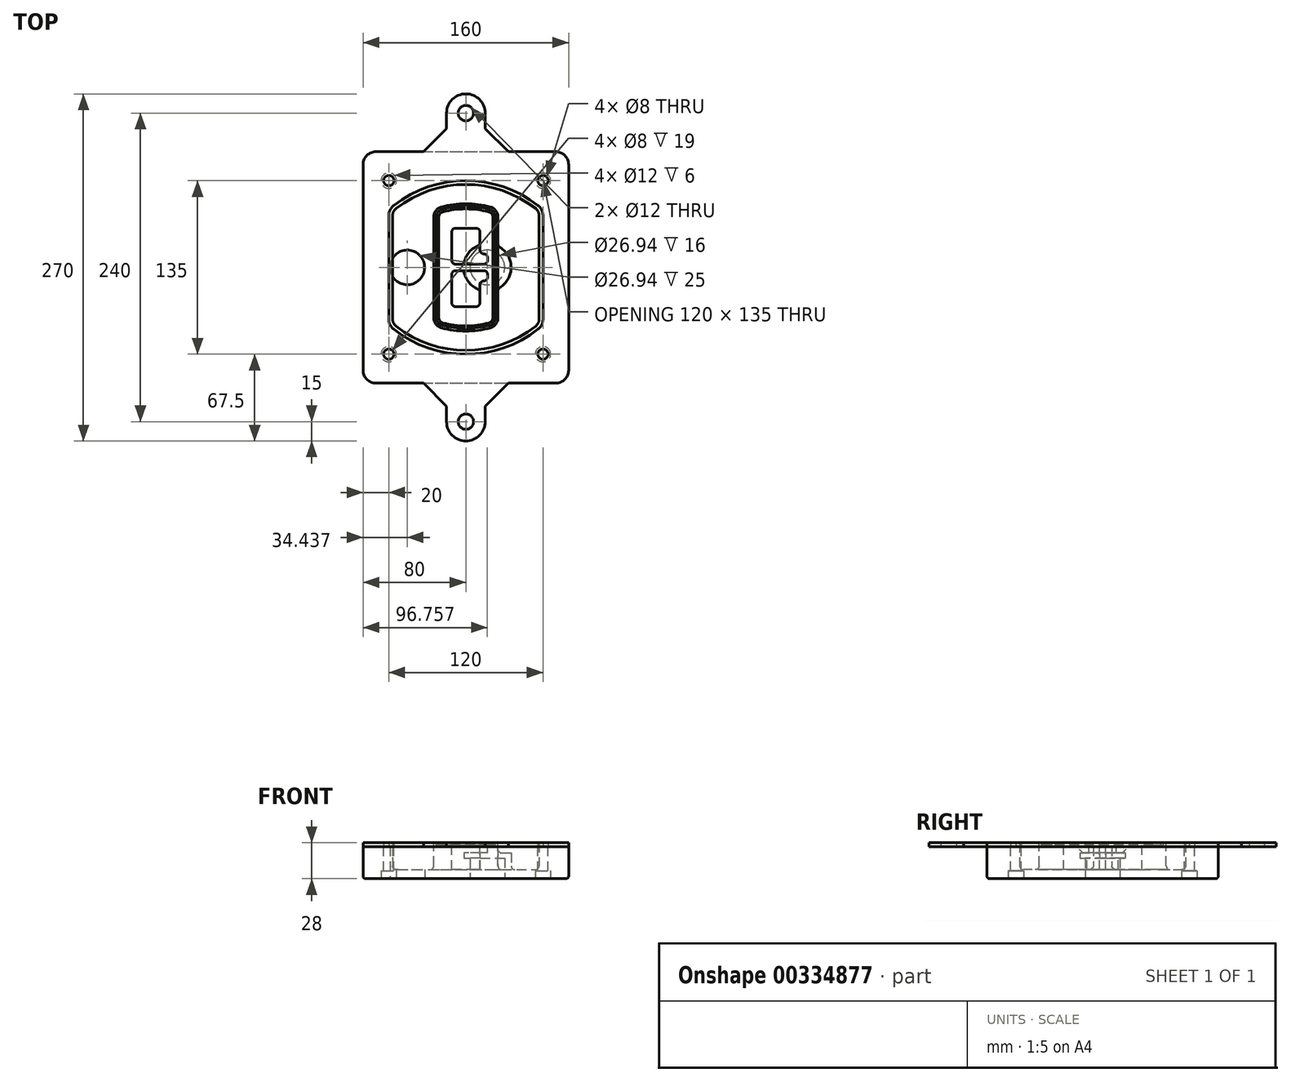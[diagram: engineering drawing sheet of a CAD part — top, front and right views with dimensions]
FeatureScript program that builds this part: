
annotation { "Feature Type Name" : "Feature", "Feature Type Description" : "" }
export const myFeature = defineFeature(function(context is Context, id is Id, definition is map)
    precondition{}
    {
        {
            var Q0;
            Q0=qCreatedBy(makeId("Top.planeOp"),FACE);
            var sketch = newSketch(context, id + "F0", { "sketchPlane" : qUnion([Q0])});
            skPoint(sketch, "E0.rect.middle", {"position": v(0, 0) * mm});
            skLineSegment(sketch, "E1.bottom", {"start": v(-70, -90) * mm, "end": v(70, -90) * mm});
            skLineSegment(sketch, "E1.top", {"start": v(-70, 90) * mm, "end": v(70, 90) * mm});
            skLineSegment(sketch, "E1.left", {"start": v(-80, -80) * mm, "end": v(-80, 80) * mm});
            skLineSegment(sketch, "E1.right", {"start": v(80, -80) * mm, "end": v(80, 80) * mm});
            skLineSegment(sketch, "E2", {"start": v(-80, 90) * mm, "end": v(80, -90) * mm, "construction": true});
            skLineSegment(sketch, "E3", {"start": v(80, 90) * mm, "end": v(-80, -90) * mm, "construction": true});
            skCircle(sketch, "E4", {"center": v(-60, 67.5) * mm, "radius": 4 * mm});
            skCircle(sketch, "E5", {"center": v(60, 67.5) * mm, "radius": 4 * mm});
            skCircle(sketch, "E6", {"center": v(60, -67.5) * mm, "radius": 4 * mm});
            skCircle(sketch, "E7", {"center": v(-60, -67.5) * mm, "radius": 4 * mm});
            skLineSegment(sketch, "E8", {"start": v(-60, 67.5) * mm, "end": v(60, 67.5) * mm, "construction": true});
            skLineSegment(sketch, "E9", {"start": v(60, 67.5) * mm, "end": v(60, -67.5) * mm, "construction": true});
            skLineSegment(sketch, "E10", {"start": v(60, -67.5) * mm, "end": v(-60, -67.5) * mm, "construction": true});
            skLineSegment(sketch, "E11", {"start": v(-60, -67.5) * mm, "end": v(-60, 67.5) * mm, "construction": true});
            skLineSegment(sketch, "E12", {"start": v(-60, 40.3) * mm, "end": v(-60, -40.3) * mm});
            skLineSegment(sketch, "E13", {"start": v(60, 40.3) * mm, "end": v(60, -40.3) * mm});
            skArc(sketch, "E14", {"start": v(56.15, 48.18) * mm, "mid": v(0, 67.5) * mm, "end": v(-56.15, 48.18) * mm});
            skArc(sketch, "E15", {"start": v(-56.15, -48.18) * mm, "mid": v(0, -67.5) * mm, "end": v(56.15, -48.18) * mm});
            skLineSegment(sketch, "E16", {"start": v(-60, 0) * mm, "end": v(60, 0) * mm, "construction": true});
            skPoint(sketch, "E17.visualSharp", {"position": v(-60, -45) * mm});
            skArc(sketch, "E17.filletArc", {"start": v(-60, -40.3) * mm, "mid": v(-58.99, -44.68) * mm, "end": v(-56.15, -48.18) * mm});
            skPoint(sketch, "E18.visualSharp", {"position": v(-60, 45) * mm});
            skArc(sketch, "E18.filletArc", {"start": v(-56.15, 48.18) * mm, "mid": v(-58.99, 44.68) * mm, "end": v(-60, 40.3) * mm});
            skPoint(sketch, "E19.visualSharp", {"position": v(60, 45) * mm});
            skArc(sketch, "E19.filletArc", {"start": v(60, 40.3) * mm, "mid": v(58.99, 44.68) * mm, "end": v(56.15, 48.18) * mm});
            skPoint(sketch, "E20.visualSharp", {"position": v(60, -45) * mm});
            skArc(sketch, "E20.filletArc", {"start": v(56.15, -48.18) * mm, "mid": v(58.99, -44.68) * mm, "end": v(60, -40.3) * mm});
            skPoint(sketch, "E21.visualSharp", {"position": v(-80, 90) * mm});
            skArc(sketch, "E21.filletArc", {"start": v(-70, 90) * mm, "mid": v(-77.07, 87.07) * mm, "end": v(-80, 80) * mm});
            skPoint(sketch, "E22.visualSharp", {"position": v(80, 90) * mm});
            skArc(sketch, "E22.filletArc", {"start": v(80, 80) * mm, "mid": v(77.07, 87.07) * mm, "end": v(70, 90) * mm});
            skPoint(sketch, "E23.visualSharp", {"position": v(80, -90) * mm});
            skArc(sketch, "E23.filletArc", {"start": v(70, -90) * mm, "mid": v(77.07, -87.07) * mm, "end": v(80, -80) * mm});
            skPoint(sketch, "E24.visualSharp", {"position": v(-80, -90) * mm});
            skArc(sketch, "E24.filletArc", {"start": v(-80, -80) * mm, "mid": v(-77.07, -87.07) * mm, "end": v(-70, -90) * mm});
            skArc(sketch, "E25.0", {"start": v(57, 40.3) * mm, "mid": v(56.3, 43.36) * mm, "end": v(54.3, 45.81) * mm});
            skLineSegment(sketch, "E25.1", {"start": v(57, 40.3) * mm, "end": v(57, -40.3) * mm});
            skArc(sketch, "E25.2", {"start": v(54.3, -45.81) * mm, "mid": v(56.3, -43.36) * mm, "end": v(57, -40.3) * mm});
            skArc(sketch, "E25.3", {"start": v(-54.3, -45.81) * mm, "mid": v(0, -64.5) * mm, "end": v(54.3, -45.81) * mm});
            skArc(sketch, "E25.4", {"start": v(-57, -40.3) * mm, "mid": v(-56.3, -43.36) * mm, "end": v(-54.3, -45.81) * mm});
            skArc(sketch, "E25.5", {"start": v(54.3, 45.81) * mm, "mid": v(0, 64.5) * mm, "end": v(-54.3, 45.81) * mm});
            skLineSegment(sketch, "E25.6", {"start": v(-57, 40.3) * mm, "end": v(-57, -40.3) * mm});
            skArc(sketch, "E25.7", {"start": v(-54.3, 45.81) * mm, "mid": v(-56.3, 43.36) * mm, "end": v(-57, 40.3) * mm});
            skArc(sketch, "E26.0", {"start": v(-58.62, 51.33) * mm, "mid": v(-62.58, 46.43) * mm, "end": v(-64, 40.3) * mm});
            skArc(sketch, "E26.1", {"start": v(58.62, 51.33) * mm, "mid": v(0, 71.5) * mm, "end": v(-58.62, 51.33) * mm});
            skArc(sketch, "E26.2", {"start": v(64, 40.3) * mm, "mid": v(62.58, 46.43) * mm, "end": v(58.62, 51.33) * mm});
            skLineSegment(sketch, "E26.3", {"start": v(64, 40.3) * mm, "end": v(64, -40.3) * mm});
            skArc(sketch, "E26.4", {"start": v(58.62, -51.33) * mm, "mid": v(62.58, -46.43) * mm, "end": v(64, -40.3) * mm});
            skLineSegment(sketch, "E26.5", {"start": v(-64, 40.3) * mm, "end": v(-64, -40.3) * mm});
            skArc(sketch, "E26.6", {"start": v(-58.62, -51.33) * mm, "mid": v(0, -71.5) * mm, "end": v(58.62, -51.33) * mm});
            skArc(sketch, "E26.7", {"start": v(-64, -40.3) * mm, "mid": v(-62.58, -46.43) * mm, "end": v(-58.62, -51.33) * mm});
            skSolve(sketch);
        }
        {
            var Q0;
            Q0=makeQuery(id+"F0.imprint","IMPRINT",FACE,{"disambiguationData":[TD([[makeQuery(id+"F0.imprint","IMPRINT",EDGE,{"derivedFrom":sQuery(id+"F0.wireOp",EDGE,"E1.bottom")}),1.0]])]});
            var Q1;
            Q1=makeQuery(id+"F0.imprint","IMPRINT",FACE,{"disambiguationData":[TD([[makeQuery(id+"F0.imprint","IMPRINT",EDGE,{"derivedFrom":sQuery(id+"F0.wireOp",EDGE,"E12")}),1.0]])]});
            var Q2;
            Q2=makeQuery(id+"F0.imprint","IMPRINT",FACE,{"disambiguationData":[TD([[makeQuery(id+"F0.imprint","IMPRINT",EDGE,{"derivedFrom":sQuery(id+"F0.wireOp",EDGE,"E25.0")}),1.0]])]});
            var Q3;
            Q3=makeQuery(id+"F0.imprint","IMPRINT",FACE,{"disambiguationData":[TD([[makeQuery(id+"F0.imprint","IMPRINT",EDGE,{"derivedFrom":sQuery(id+"F0.wireOp",EDGE,"E12")}),-1.0]])]});
            extrude(context, id + "F1", {"entities" : qUnion([Q0, Q1, Q2, Q3]), "oppositeDirection" : true, "depth" : 25 * mm});
        }
        {
            var Q0;
            Q0=makeQuery(id+"F0.imprint","IMPRINT",FACE,{"disambiguationData":[TD([[makeQuery(id+"F0.imprint","IMPRINT",EDGE,{"derivedFrom":sQuery(id+"F0.wireOp",EDGE,"E12")}),1.0]])]});
            extrude(context, id + "F2", {"entities" : qUnion([Q0]), "operationType" : NewBodyOperationType.ADD, "depth" : 3 * mm});
        }
        {
            var Q0;
            Q0=makeQuery(id+"F0.imprint","IMPRINT",FACE,{"disambiguationData":[TD([[makeQuery(id+"F0.imprint","IMPRINT",EDGE,{"derivedFrom":sQuery(id+"F0.wireOp",EDGE,"E25.0")}),1.0]])]});
            extrude(context, id + "F3", {"entities" : qUnion([Q0]), "operationType" : NewBodyOperationType.REMOVE, "oppositeDirection" : true, "depth" : 18 * mm});
        }
        {
            var Q0;
            Q0=makeQuery(id+"F2.opExtrude","CAP_FACE",FACE,{"disambiguationData":[OSD([sQuery(id+"F0.wireOp",EDGE,"E12"),sQuery(id+"F0.wireOp",EDGE,"E13"),sQuery(id+"F0.wireOp",EDGE,"E14"),sQuery(id+"F0.wireOp",EDGE,"E15"),sQuery(id+"F0.wireOp",EDGE,"E17.filletArc"),sQuery(id+"F0.wireOp",EDGE,"E18.filletArc"),sQuery(id+"F0.wireOp",EDGE,"E19.filletArc"),sQuery(id+"F0.wireOp",EDGE,"E20.filletArc"),sQuery(id+"F0.wireOp",EDGE,"E25.0"),sQuery(id+"F0.wireOp",EDGE,"E25.1"),sQuery(id+"F0.wireOp",EDGE,"E25.2"),sQuery(id+"F0.wireOp",EDGE,"E25.3"),sQuery(id+"F0.wireOp",EDGE,"E25.4"),sQuery(id+"F0.wireOp",EDGE,"E25.5"),sQuery(id+"F0.wireOp",EDGE,"E25.6"),sQuery(id+"F0.wireOp",EDGE,"E25.7")])],"isStart":false});
            var sketch = newSketch(context, id + "F4", { "sketchPlane" : qUnion([Q0])});
            skArc(sketch, "E27.0", {"start": v(-19.08, -46.97) * mm, "mid": v(0, -49.5) * mm, "end": v(19.08, -46.97) * mm});
            skArc(sketch, "E28.0", {"start": v(19.08, 46.97) * mm, "mid": v(0, 49.5) * mm, "end": v(-19.08, 46.97) * mm});
            skLineSegment(sketch, "E29", {"start": v(-25, 39.25) * mm, "end": v(-25, -39.25) * mm});
            skLineSegment(sketch, "E30", {"start": v(25, 39.25) * mm, "end": v(25, -39.25) * mm});
            skLineSegment(sketch, "E31", {"start": v(-25, 45.1) * mm, "end": v(25, 45.1) * mm, "construction": true});
            skLineSegment(sketch, "E32", {"start": v(-25, -45.1) * mm, "end": v(25, -45.1) * mm, "construction": true});
            skPoint(sketch, "E33.visualSharp", {"position": v(-25, 45.1) * mm});
            skArc(sketch, "E33.filletArc", {"start": v(-19.08, 46.97) * mm, "mid": v(-23.35, 44.11) * mm, "end": v(-25, 39.25) * mm});
            skPoint(sketch, "E34.visualSharp", {"position": v(25, 45.1) * mm});
            skArc(sketch, "E34.filletArc", {"start": v(25, 39.25) * mm, "mid": v(23.35, 44.11) * mm, "end": v(19.08, 46.97) * mm});
            skPoint(sketch, "E35.visualSharp", {"position": v(25, -45.1) * mm});
            skArc(sketch, "E35.filletArc", {"start": v(19.08, -46.97) * mm, "mid": v(23.35, -44.11) * mm, "end": v(25, -39.25) * mm});
            skPoint(sketch, "E36.visualSharp", {"position": v(-25, -45.1) * mm});
            skArc(sketch, "E36.filletArc", {"start": v(-25, -39.25) * mm, "mid": v(-23.35, -44.11) * mm, "end": v(-19.08, -46.97) * mm});
            skArc(sketch, "E37.0", {"start": v(54.3, 45.81) * mm, "mid": v(0, 64.5) * mm, "end": v(-54.3, 45.81) * mm});
            skArc(sketch, "E37.1", {"start": v(-54.3, 45.81) * mm, "mid": v(-56.3, 43.36) * mm, "end": v(-57, 40.3) * mm});
            skLineSegment(sketch, "E37.2", {"start": v(-57, 40.3) * mm, "end": v(-57, -40.3) * mm});
            skArc(sketch, "E37.3", {"start": v(-57, -40.3) * mm, "mid": v(-56.3, -43.36) * mm, "end": v(-54.3, -45.81) * mm});
            skArc(sketch, "E37.4", {"start": v(-54.3, -45.81) * mm, "mid": v(0, -64.5) * mm, "end": v(54.3, -45.81) * mm});
            skArc(sketch, "E37.5", {"start": v(54.3, -45.81) * mm, "mid": v(56.3, -43.36) * mm, "end": v(57, -40.3) * mm});
            skLineSegment(sketch, "E37.6", {"start": v(57, 40.3) * mm, "end": v(57, -40.3) * mm});
            skArc(sketch, "E37.7", {"start": v(57, 40.3) * mm, "mid": v(56.3, 43.36) * mm, "end": v(54.3, 45.81) * mm});
            skLineSegment(sketch, "E38.0", {"start": v(23, 39.25) * mm, "end": v(23, -39.25) * mm});
            skArc(sketch, "E38.1", {"start": v(18.56, -45.04) * mm, "mid": v(21.76, -42.9) * mm, "end": v(23, -39.25) * mm});
            skArc(sketch, "E38.2", {"start": v(-18.56, -45.04) * mm, "mid": v(0, -47.5) * mm, "end": v(18.56, -45.04) * mm});
            skArc(sketch, "E38.3", {"start": v(-23, -39.25) * mm, "mid": v(-21.76, -42.9) * mm, "end": v(-18.56, -45.04) * mm});
            skLineSegment(sketch, "E38.4", {"start": v(-23, 39.25) * mm, "end": v(-23, -39.25) * mm});
            skArc(sketch, "E38.5", {"start": v(23, 39.25) * mm, "mid": v(21.76, 42.9) * mm, "end": v(18.56, 45.04) * mm});
            skArc(sketch, "E38.6", {"start": v(-18.56, 45.04) * mm, "mid": v(-21.76, 42.9) * mm, "end": v(-23, 39.25) * mm});
            skArc(sketch, "E38.7", {"start": v(18.56, 45.04) * mm, "mid": v(0, 47.5) * mm, "end": v(-18.56, 45.04) * mm});
            skArc(sketch, "E39.0", {"start": v(21, 39.25) * mm, "mid": v(20.18, 41.68) * mm, "end": v(18.04, 43.1) * mm});
            skLineSegment(sketch, "E39.1", {"start": v(21, 39.25) * mm, "end": v(21, -39.25) * mm});
            skArc(sketch, "E39.2", {"start": v(18.04, -43.1) * mm, "mid": v(20.18, -41.68) * mm, "end": v(21, -39.25) * mm});
            skArc(sketch, "E39.3", {"start": v(-18.04, -43.1) * mm, "mid": v(0, -45.5) * mm, "end": v(18.04, -43.1) * mm});
            skArc(sketch, "E39.4", {"start": v(-21, -39.25) * mm, "mid": v(-20.18, -41.68) * mm, "end": v(-18.04, -43.1) * mm});
            skArc(sketch, "E39.5", {"start": v(18.04, 43.1) * mm, "mid": v(0, 45.5) * mm, "end": v(-18.04, 43.1) * mm});
            skLineSegment(sketch, "E39.6", {"start": v(-21, 39.25) * mm, "end": v(-21, -39.25) * mm});
            skArc(sketch, "E39.7", {"start": v(-18.04, 43.1) * mm, "mid": v(-20.18, 41.68) * mm, "end": v(-21, 39.25) * mm});
            skLineSegment(sketch, "E40", {"start": v(-25, 0) * mm, "end": v(25, 0) * mm, "construction": true});
            skLineSegment(sketch, "E41", {"start": v(-11, 5.5) * mm, "end": v(-11, 27.5) * mm});
            skLineSegment(sketch, "E42", {"start": v(-8, 30.5) * mm, "end": v(8, 30.5) * mm});
            skLineSegment(sketch, "E43", {"start": v(11, 27.5) * mm, "end": v(11, 13.5) * mm});
            skLineSegment(sketch, "E44", {"start": v(14, 10.5) * mm, "end": v(14, 10.5) * mm});
            skLineSegment(sketch, "E45", {"start": v(17, 7.5) * mm, "end": v(17, 5.5) * mm});
            skLineSegment(sketch, "E46", {"start": v(14, 2.5) * mm, "end": v(-8, 2.5) * mm});
            skPoint(sketch, "E47.visualSharp", {"position": v(-11, 30.5) * mm});
            skArc(sketch, "E47.filletArc", {"start": v(-8, 30.5) * mm, "mid": v(-10.12, 29.62) * mm, "end": v(-11, 27.5) * mm});
            skPoint(sketch, "E48.visualSharp", {"position": v(11, 30.5) * mm});
            skArc(sketch, "E48.filletArc", {"start": v(11, 27.5) * mm, "mid": v(10.12, 29.62) * mm, "end": v(8, 30.5) * mm});
            skPoint(sketch, "E49.visualSharp", {"position": v(11, 10.5) * mm});
            skArc(sketch, "E49.filletArc", {"start": v(11, 13.5) * mm, "mid": v(11.88, 11.38) * mm, "end": v(14, 10.5) * mm});
            skPoint(sketch, "E50.visualSharp", {"position": v(17, 10.5) * mm});
            skArc(sketch, "E50.filletArc", {"start": v(17, 7.5) * mm, "mid": v(16.12, 9.62) * mm, "end": v(14, 10.5) * mm});
            skPoint(sketch, "E51.visualSharp", {"position": v(17, 2.5) * mm});
            skArc(sketch, "E51.filletArc", {"start": v(14, 2.5) * mm, "mid": v(16.12, 3.38) * mm, "end": v(17, 5.5) * mm});
            skPoint(sketch, "E52.visualSharp", {"position": v(-11, 2.5) * mm});
            skArc(sketch, "E52.filletArc", {"start": v(-11, 5.5) * mm, "mid": v(-10.12, 3.38) * mm, "end": v(-8, 2.5) * mm});
            skLineSegment(sketch, "E53.0.MirrorCS", {"start": v(14, -2.5) * mm, "end": v(-8, -2.5) * mm});
            skArc(sketch, "E54.0.MirrorCS", {"start": v(-11, -5.5) * mm, "mid": v(-10.12, -3.38) * mm, "end": v(-8, -2.5) * mm});
            skLineSegment(sketch, "E55.0.MirrorCS", {"start": v(-11, -5.5) * mm, "end": v(-11, -27.5) * mm});
            skArc(sketch, "E56.0.MirrorCS", {"start": v(-8, -30.5) * mm, "mid": v(-10.12, -29.62) * mm, "end": v(-11, -27.5) * mm});
            skLineSegment(sketch, "E57.0.MirrorCS", {"start": v(-8, -30.5) * mm, "end": v(8, -30.5) * mm});
            skArc(sketch, "E58.0.MirrorCS", {"start": v(11, -27.5) * mm, "mid": v(10.12, -29.62) * mm, "end": v(8, -30.5) * mm});
            skLineSegment(sketch, "E59.0.MirrorCS", {"start": v(11, -27.5) * mm, "end": v(11, -13.5) * mm});
            skArc(sketch, "E60.0.MirrorCS", {"start": v(11, -13.5) * mm, "mid": v(11.88, -11.38) * mm, "end": v(14, -10.5) * mm});
            skArc(sketch, "E61.0.MirrorCS", {"start": v(17, -7.5) * mm, "mid": v(16.12, -9.62) * mm, "end": v(14, -10.5) * mm});
            skLineSegment(sketch, "E62.0.MirrorCS", {"start": v(17, -7.5) * mm, "end": v(17, -5.5) * mm});
            skArc(sketch, "E63.0.MirrorCS", {"start": v(14, -2.5) * mm, "mid": v(16.12, -3.38) * mm, "end": v(17, -5.5) * mm});
            skSolve(sketch);
        }
        {
            var Q0;
            Q0=makeQuery(id+"F4.imprint","IMPRINT",FACE,{"disambiguationData":[TD([[makeQuery(id+"F4.imprint","IMPRINT",EDGE,{"derivedFrom":sQuery(id+"F4.wireOp",EDGE,"E27.0")}),1.0]])]});
            var Q1;
            Q1=makeQuery(id+"F4.imprint","IMPRINT",FACE,{"disambiguationData":[TD([[makeQuery(id+"F4.imprint","IMPRINT",EDGE,{"derivedFrom":sQuery(id+"F4.wireOp",EDGE,"E38.0")}),-1.0]])]});
            var Q2;
            Q2=makeQuery(id+"F4.imprint","IMPRINT",FACE,{"disambiguationData":[TD([[makeQuery(id+"F4.imprint","IMPRINT",EDGE,{"derivedFrom":sQuery(id+"F4.wireOp",EDGE,"E39.0")}),1.0]])]});
            extrude(context, id + "F5", {"entities" : qUnion([Q0, Q1, Q2]), "operationType" : NewBodyOperationType.ADD, "endBound" : BoundingType.UP_TO_NEXT, "oppositeDirection" : true, "depth" : 25 * mm});
        }
        {
            var Q0;
            Q0=makeQuery(id+"F4.imprint","IMPRINT",FACE,{"disambiguationData":[TD([[makeQuery(id+"F4.imprint","IMPRINT",EDGE,{"derivedFrom":sQuery(id+"F4.wireOp",EDGE,"E38.0")}),-1.0]])]});
            extrude(context, id + "F6", {"entities" : qUnion([Q0]), "operationType" : NewBodyOperationType.REMOVE, "oppositeDirection" : true, "depth" : 2 * mm});
        }
        {
            var Q0;
            Q0=makeQuery(id+"F1.opExtrude","CAP_FACE",FACE,{"disambiguationData":[OSD([sQuery(id+"F0.wireOp",EDGE,"E1.bottom"),sQuery(id+"F0.wireOp",EDGE,"E1.top"),sQuery(id+"F0.wireOp",EDGE,"E1.left"),sQuery(id+"F0.wireOp",EDGE,"E1.right"),sQuery(id+"F0.wireOp",EDGE,"E4"),sQuery(id+"F0.wireOp",EDGE,"E5"),sQuery(id+"F0.wireOp",EDGE,"E6"),sQuery(id+"F0.wireOp",EDGE,"E7"),sQuery(id+"F0.wireOp",EDGE,"E21.filletArc"),sQuery(id+"F0.wireOp",EDGE,"E22.filletArc"),sQuery(id+"F0.wireOp",EDGE,"E23.filletArc"),sQuery(id+"F0.wireOp",EDGE,"E24.filletArc")])],"isStart":false});
            var sketch = newSketch(context, id + "F7", { "sketchPlane" : qUnion([Q0])});
            skCircle(sketch, "E64", {"center": v(16.76, 0) * mm, "radius": 13.47 * mm});
            skCircle(sketch, "E65", {"center": v(-45.56, 0) * mm, "radius": 13.47 * mm});
            skLineSegment(sketch, "E66", {"start": v(80, 0) * mm, "end": v(-80, 0) * mm});
            skCircle(sketch, "E67", {"center": v(16.76, 0) * mm, "radius": 18.47 * mm});
            skCircle(sketch, "E68", {"center": v(60, -67.5) * mm, "radius": 6 * mm});
            skCircle(sketch, "E69", {"center": v(-60, -67.5) * mm, "radius": 6 * mm});
            skCircle(sketch, "E70", {"center": v(-60, 67.5) * mm, "radius": 6 * mm});
            skCircle(sketch, "E71", {"center": v(60, 67.5) * mm, "radius": 6 * mm});
            skSolve(sketch);
        }
        {
            var Q0;
            {var subQ1=sQuery(id+"F7.wireOp",EDGE,"E66");var subQ4=sQuery(id+"F7.wireOp",EDGE,"E64");var subQ6=makeQuery(id+"F7.imprint","INTERSECT",VERTEX,{"disambiguationData":[OD(0.0)],"derivedFrom":[subQ4,subQ1]});Q0=makeQuery(id+"F7.imprint","IMPRINT",FACE,{"disambiguationData":[TD([[makeQuery(id+"F7.imprint","IMPRINT",EDGE,{"disambiguationData":[TD([[subQ6,-1.0]])],"derivedFrom":subQ4}),-1.0]])]});}
            var Q1;
            {var subQ0=sQuery(id+"F7.wireOp",EDGE,"E66");var subQ1=sQuery(id+"F7.wireOp",EDGE,"E64");var subQ3=makeQuery(id+"F7.imprint","INTERSECT",VERTEX,{"disambiguationData":[OD(0.0)],"derivedFrom":[subQ1,subQ0]});Q1=makeQuery(id+"F7.imprint","IMPRINT",FACE,{"disambiguationData":[TD([[makeQuery(id+"F7.imprint","IMPRINT",EDGE,{"disambiguationData":[TD([[subQ3,-1.0]])],"derivedFrom":subQ1}),1.0]])]});}
            var Q2;
            {var subQ0=sQuery(id+"F7.wireOp",EDGE,"E66");var subQ1=sQuery(id+"F7.wireOp",EDGE,"E64");var subQ3=makeQuery(id+"F7.imprint","INTERSECT",VERTEX,{"disambiguationData":[OD(0.0)],"derivedFrom":[subQ1,subQ0]});Q2=makeQuery(id+"F7.imprint","IMPRINT",FACE,{"disambiguationData":[TD([[makeQuery(id+"F7.imprint","IMPRINT",EDGE,{"disambiguationData":[TD([[subQ3,1.0]])],"derivedFrom":subQ1}),1.0]])]});}
            var Q3;
            {var subQ1=sQuery(id+"F7.wireOp",EDGE,"E66");var subQ4=sQuery(id+"F7.wireOp",EDGE,"E64");var subQ6=makeQuery(id+"F7.imprint","INTERSECT",VERTEX,{"disambiguationData":[OD(0.0)],"derivedFrom":[subQ4,subQ1]});Q3=makeQuery(id+"F7.imprint","IMPRINT",FACE,{"disambiguationData":[TD([[makeQuery(id+"F7.imprint","IMPRINT",EDGE,{"disambiguationData":[TD([[subQ6,1.0]])],"derivedFrom":subQ4}),-1.0]])]});}
            extrude(context, id + "F8", {"entities" : qUnion([Q0, Q1, Q2, Q3]), "operationType" : NewBodyOperationType.ADD, "oppositeDirection" : true, "depth" : 20 * mm});
        }
        {
            var Q0;
            {var subQ0=sQuery(id+"F7.wireOp",EDGE,"E66");var subQ1=sQuery(id+"F7.wireOp",EDGE,"E64");var subQ3=makeQuery(id+"F7.imprint","INTERSECT",VERTEX,{"disambiguationData":[OD(0.0)],"derivedFrom":[subQ1,subQ0]});Q0=makeQuery(id+"F7.imprint","IMPRINT",FACE,{"disambiguationData":[TD([[makeQuery(id+"F7.imprint","IMPRINT",EDGE,{"disambiguationData":[TD([[subQ3,-1.0]])],"derivedFrom":subQ1}),1.0]])]});}
            var Q1;
            {var subQ0=sQuery(id+"F7.wireOp",EDGE,"E66");var subQ1=sQuery(id+"F7.wireOp",EDGE,"E64");var subQ3=makeQuery(id+"F7.imprint","INTERSECT",VERTEX,{"disambiguationData":[OD(0.0)],"derivedFrom":[subQ1,subQ0]});Q1=makeQuery(id+"F7.imprint","IMPRINT",FACE,{"disambiguationData":[TD([[makeQuery(id+"F7.imprint","IMPRINT",EDGE,{"disambiguationData":[TD([[subQ3,1.0]])],"derivedFrom":subQ1}),1.0]])]});}
            extrude(context, id + "F9", {"entities" : qUnion([Q0, Q1]), "operationType" : NewBodyOperationType.REMOVE, "oppositeDirection" : true, "depth" : 16 * mm});
        }
        {
            var Q0;
            {var subQ0=sQuery(id+"F7.wireOp",EDGE,"E66");var subQ1=sQuery(id+"F7.wireOp",EDGE,"E65");var subQ3=makeQuery(id+"F7.imprint","INTERSECT",VERTEX,{"disambiguationData":[OD(0.0)],"derivedFrom":[subQ1,subQ0]});Q0=makeQuery(id+"F7.imprint","IMPRINT",FACE,{"disambiguationData":[TD([[makeQuery(id+"F7.imprint","IMPRINT",EDGE,{"disambiguationData":[TD([[subQ3,-1.0]])],"derivedFrom":subQ1}),1.0]])]});}
            var Q1;
            {var subQ0=sQuery(id+"F7.wireOp",EDGE,"E66");var subQ1=sQuery(id+"F7.wireOp",EDGE,"E65");var subQ3=makeQuery(id+"F7.imprint","INTERSECT",VERTEX,{"disambiguationData":[OD(0.0)],"derivedFrom":[subQ1,subQ0]});Q1=makeQuery(id+"F7.imprint","IMPRINT",FACE,{"disambiguationData":[TD([[makeQuery(id+"F7.imprint","IMPRINT",EDGE,{"disambiguationData":[TD([[subQ3,1.0]])],"derivedFrom":subQ1}),1.0]])]});}
            extrude(context, id + "F10", {"entities" : qUnion([Q0, Q1]), "operationType" : NewBodyOperationType.REMOVE, "oppositeDirection" : true, "depth" : 25 * mm});
        }
        {
            var Q0;
            Q0=makeQuery(id+"F7.imprint","IMPRINT",FACE,{"disambiguationData":[TD([[makeQuery(id+"F7.imprint","IMPRINT",EDGE,{"derivedFrom":sQuery(id+"F7.wireOp",EDGE,"E68")}),1.0]])]});
            var Q1;
            Q1=makeQuery(id+"F7.imprint","IMPRINT",FACE,{"disambiguationData":[TD([[makeQuery(id+"F7.imprint","IMPRINT",EDGE,{"derivedFrom":makeQuery(id+"F1.opExtrude","CAP_EDGE",EDGE,{"disambiguationData":[OSD([sQuery(id+"F0.wireOp",EDGE,"E5")])],"isStart":false})}),-1.0]])]});
            var Q2;
            Q2=makeQuery(id+"F7.imprint","IMPRINT",FACE,{"disambiguationData":[TD([[makeQuery(id+"F7.imprint","IMPRINT",EDGE,{"derivedFrom":sQuery(id+"F7.wireOp",EDGE,"E69")}),1.0]])]});
            var Q3;
            Q3=makeQuery(id+"F7.imprint","IMPRINT",FACE,{"disambiguationData":[TD([[makeQuery(id+"F7.imprint","IMPRINT",EDGE,{"derivedFrom":makeQuery(id+"F1.opExtrude","CAP_EDGE",EDGE,{"disambiguationData":[OSD([sQuery(id+"F0.wireOp",EDGE,"E4")])],"isStart":false})}),-1.0]])]});
            var Q4;
            Q4=makeQuery(id+"F7.imprint","IMPRINT",FACE,{"disambiguationData":[TD([[makeQuery(id+"F7.imprint","IMPRINT",EDGE,{"derivedFrom":sQuery(id+"F7.wireOp",EDGE,"E70")}),1.0]])]});
            var Q5;
            Q5=makeQuery(id+"F7.imprint","IMPRINT",FACE,{"disambiguationData":[TD([[makeQuery(id+"F7.imprint","IMPRINT",EDGE,{"derivedFrom":makeQuery(id+"F1.opExtrude","CAP_EDGE",EDGE,{"disambiguationData":[OSD([sQuery(id+"F0.wireOp",EDGE,"E7")])],"isStart":false})}),-1.0]])]});
            var Q6;
            Q6=makeQuery(id+"F7.imprint","IMPRINT",FACE,{"disambiguationData":[TD([[makeQuery(id+"F7.imprint","IMPRINT",EDGE,{"derivedFrom":sQuery(id+"F7.wireOp",EDGE,"E71")}),1.0]])]});
            var Q7;
            Q7=makeQuery(id+"F7.imprint","IMPRINT",FACE,{"disambiguationData":[TD([[makeQuery(id+"F7.imprint","IMPRINT",EDGE,{"derivedFrom":makeQuery(id+"F1.opExtrude","CAP_EDGE",EDGE,{"disambiguationData":[OSD([sQuery(id+"F0.wireOp",EDGE,"E6")])],"isStart":false})}),-1.0]])]});
            extrude(context, id + "F11", {"entities" : qUnion([Q0, Q1, Q2, Q3, Q4, Q5, Q6, Q7]), "operationType" : NewBodyOperationType.REMOVE, "oppositeDirection" : true, "depth" : 6 * mm});
        }
        {
            var Q0;
            Q0=makeQuery(id+"F9.boolean.opBoolean","COPY",FACE,{"derivedFrom":makeQuery(id+"F9.opExtrude","CAP_FACE",FACE,{"disambiguationData":[OSD([sQuery(id+"F7.wireOp",EDGE,"E64")])],"isStart":false})});
            var sketch = newSketch(context, id + "F12", { "sketchPlane" : qUnion([Q0])});
            skArc(sketch, "E72.0", {"start": v(11, 17.55) * mm, "mid": v(2.57, 11.82) * mm, "end": v(-1.54, 2.5) * mm});
            skArc(sketch, "E72.1", {"start": v(-1.54, -2.5) * mm, "mid": v(2.57, -11.82) * mm, "end": v(11, -17.55) * mm});
            skLineSegment(sketch, "E73", {"start": v(-1.54, -2.5) * mm, "end": v(14, -2.5) * mm});
            skLineSegment(sketch, "E74.0", {"start": v(14, 2.5) * mm, "end": v(-1.54, 2.5) * mm});
            skArc(sketch, "E74.1", {"start": v(14, 2.5) * mm, "mid": v(16.12, 3.38) * mm, "end": v(17, 5.5) * mm});
            skLineSegment(sketch, "E74.2", {"start": v(17, 7.5) * mm, "end": v(17, 5.5) * mm});
            skArc(sketch, "E74.3", {"start": v(17, 7.5) * mm, "mid": v(16.12, 9.62) * mm, "end": v(14, 10.5) * mm});
            skArc(sketch, "E74.4", {"start": v(11, 13.5) * mm, "mid": v(11.88, 11.38) * mm, "end": v(14, 10.5) * mm});
            skLineSegment(sketch, "E74.5", {"start": v(11, 17.55) * mm, "end": v(11, 13.5) * mm});
            skLineSegment(sketch, "E74.7", {"start": v(14, -2.5) * mm, "end": v(-1.54, -2.5) * mm});
            skArc(sketch, "E74.8", {"start": v(14, -2.5) * mm, "mid": v(16.12, -3.38) * mm, "end": v(17, -5.5) * mm});
            skLineSegment(sketch, "E74.9", {"start": v(17, -7.5) * mm, "end": v(17, -5.5) * mm});
            skArc(sketch, "E74.10", {"start": v(17, -7.5) * mm, "mid": v(16.12, -9.62) * mm, "end": v(14, -10.5) * mm});
            skArc(sketch, "E74.11", {"start": v(11, -13.5) * mm, "mid": v(11.88, -11.38) * mm, "end": v(14, -10.5) * mm});
            skLineSegment(sketch, "E74.12", {"start": v(11, -17.55) * mm, "end": v(11, -13.5) * mm});
            skPoint(sketch, "E75.orphan", {"position": v(11, -27.5) * mm});
            skPoint(sketch, "E76.orphan", {"position": v(-8, -2.5) * mm});
            skPoint(sketch, "E77.orphan", {"position": v(-8, 2.5) * mm});
            skPoint(sketch, "E78.orphan", {"position": v(11, 27.5) * mm});
            skSolve(sketch);
        }
        {
            var Q0;
            {var subQ7=sQuery(id+"F12.wireOp",EDGE,"E72.0");var subQ14=sQuery(id+"F12.wireOp",EDGE,"E72.1");var subQ16=sQuery(id+"F12.wireOp",EDGE,"E74.1");var subQ18=sQuery(id+"F12.wireOp",EDGE,"E74.8");Q0=qUnion([makeQuery(id+"F12.imprint","IMPRINT",FACE,{"disambiguationData":[TD([[makeQuery(id+"F12.imprint","IMPRINT",EDGE,{"derivedFrom":subQ7}),1.0]])]}),makeQuery(id+"F12.imprint","IMPRINT",FACE,{"disambiguationData":[TD([[makeQuery(id+"F12.imprint","IMPRINT",EDGE,{"derivedFrom":subQ14}),1.0]])]}),makeQuery(id+"F12.imprint","IMPRINT",FACE,{"disambiguationData":[TD([[makeQuery(id+"F12.imprint","IMPRINT",EDGE,{"derivedFrom":subQ16}),1.0]])]}),makeQuery(id+"F12.imprint","IMPRINT",FACE,{"disambiguationData":[TD([[makeQuery(id+"F12.imprint","IMPRINT",EDGE,{"derivedFrom":subQ18}),-1.0]])]})]);}
            var Q1;
            Q1=makeQuery(id+"F5.boolean.opBoolean","SPLIT",FACE,{"disambiguationData":[TD([makeQuery(id+"F5.opExtrude","SWEPT_FACE",FACE,{"disambiguationData":[OSD([sQuery(id+"F4.wireOp",EDGE,"E41")])]})])],"derivedFrom":makeQuery(id+"F3.boolean.opBoolean","COPY",FACE,{"derivedFrom":makeQuery(id+"F3.opExtrude","CAP_FACE",FACE,{"disambiguationData":[OSD([sQuery(id+"F0.wireOp",EDGE,"E25.0"),sQuery(id+"F0.wireOp",EDGE,"E25.1"),sQuery(id+"F0.wireOp",EDGE,"E25.2"),sQuery(id+"F0.wireOp",EDGE,"E25.3"),sQuery(id+"F0.wireOp",EDGE,"E25.4"),sQuery(id+"F0.wireOp",EDGE,"E25.5"),sQuery(id+"F0.wireOp",EDGE,"E25.6"),sQuery(id+"F0.wireOp",EDGE,"E25.7")])],"isStart":false})})});
            extrude(context, id + "F13", {"entities" : qUnion([Q0]), "operationType" : NewBodyOperationType.REMOVE, "endBound" : BoundingType.UP_TO_SURFACE, "endBoundEntityFace" : qUnion([Q1]), "depth" : 25 * mm});
        }
        {
            var Q0;
            Q0=makeQuery(id+"F3.boolean.opBoolean","COPY",EDGE,{"derivedFrom":makeQuery(id+"F3.opExtrude","CAP_EDGE",EDGE,{"disambiguationData":[OSD([sQuery(id+"F0.wireOp",EDGE,"E25.6")])],"isStart":false})});
            var Q1;
            Q1=makeQuery(id+"F8.boolean.opBoolean","INTERSECT",EDGE,{"derivedFrom":[makeQuery(id+"F5.opExtrude","SWEPT_FACE",FACE,{"disambiguationData":[OSD([sQuery(id+"F4.wireOp",EDGE,"E30")])]}),makeQuery(id+"F8.opExtrude","CAP_FACE",FACE,{"disambiguationData":[OSD([sQuery(id+"F7.wireOp",EDGE,"E67")])],"isStart":false})]});
            var Q2;
            Q2=makeQuery(id+"F8.boolean.opBoolean","INTERSECT",EDGE,{"disambiguationData":[OD(1.0)],"derivedFrom":[makeQuery(id+"F5.opExtrude","SWEPT_FACE",FACE,{"disambiguationData":[OSD([sQuery(id+"F4.wireOp",EDGE,"E30")])]}),makeQuery(id+"F8.opExtrude","SWEPT_FACE",FACE,{"disambiguationData":[OSD([sQuery(id+"F7.wireOp",EDGE,"E67")])]})]});
            var Q3;
            {var subQ0=sQuery(id+"F4.wireOp",EDGE,"E30");Q3=makeQuery(id+"F8.boolean.opBoolean","SPLIT",EDGE,{"disambiguationData":[TD([makeQuery(id+"F5.opExtrude","SWEPT_FACE",FACE,{"disambiguationData":[OSD([sQuery(id+"F4.wireOp",EDGE,"E35.filletArc")])]})])],"derivedFrom":makeQuery(id+"F5.opExtrude","CAP_EDGE",EDGE,{"disambiguationData":[OSD([subQ0])],"isStart":false})});}
            var Q4;
            {var subQ0=sQuery(id+"F0.wireOp",EDGE,"E25.7");var subQ1=sQuery(id+"F0.wireOp",EDGE,"E25.1");var subQ2=sQuery(id+"F0.wireOp",EDGE,"E25.6");var subQ3=sQuery(id+"F0.wireOp",EDGE,"E25.5");var subQ4=sQuery(id+"F0.wireOp",EDGE,"E25.4");var subQ5=sQuery(id+"F0.wireOp",EDGE,"E25.0");var subQ6=sQuery(id+"F0.wireOp",EDGE,"E25.2");var subQ7=sQuery(id+"F0.wireOp",EDGE,"E25.3");Q4=makeQuery(id+"F8.boolean.opBoolean","INTERSECT",EDGE,{"derivedFrom":[makeQuery(id+"F5.boolean.opBoolean","SPLIT",FACE,{"disambiguationData":[TD([makeQuery(id+"F2.opExtrude","SWEPT_FACE",FACE,{"disambiguationData":[OSD([subQ5])]})])],"derivedFrom":makeQuery(id+"F3.boolean.opBoolean","COPY",FACE,{"derivedFrom":makeQuery(id+"F3.opExtrude","CAP_FACE",FACE,{"disambiguationData":[OSD([subQ5,subQ1,subQ6,subQ7,subQ4,subQ3,subQ2,subQ0])],"isStart":false})})}),makeQuery(id+"F8.opExtrude","SWEPT_FACE",FACE,{"disambiguationData":[OSD([sQuery(id+"F7.wireOp",EDGE,"E67")])]})]});}
            var Q5;
            Q5=makeQuery(id+"F8.boolean.opBoolean","INTERSECT",EDGE,{"disambiguationData":[OD(0.0)],"derivedFrom":[makeQuery(id+"F5.opExtrude","SWEPT_FACE",FACE,{"disambiguationData":[OSD([sQuery(id+"F4.wireOp",EDGE,"E30")])]}),makeQuery(id+"F8.opExtrude","SWEPT_FACE",FACE,{"disambiguationData":[OSD([sQuery(id+"F7.wireOp",EDGE,"E67")])]})]});
            fillet(context, id + "F14", {"entities" : qUnion([Q0, Q1, Q2, Q3, Q4, Q5]), "radius" : 3 * mm, "tangentPropagation" : true, "allowEdgeOverflow" : false});
        }
        {
            var Q0;
            Q0=makeQuery(id+"F1.opExtrude","CAP_EDGE",EDGE,{"disambiguationData":[OSD([sQuery(id+"F0.wireOp",EDGE,"E1.bottom")])],"isStart":false});
            fillet(context, id + "F15", {"entities" : qUnion([Q0]), "radius" : 2 * mm, "tangentPropagation" : true, "allowEdgeOverflow" : false});
        }
        {
            var Q0;
            {var subQ0=sQuery(id+"F0.wireOp",EDGE,"E21.filletArc");var subQ1=sQuery(id+"F0.wireOp",EDGE,"E7");var subQ2=sQuery(id+"F0.wireOp",EDGE,"E6");var subQ3=sQuery(id+"F0.wireOp",EDGE,"E5");var subQ4=sQuery(id+"F0.wireOp",EDGE,"E4");var subQ5=sQuery(id+"F0.wireOp",EDGE,"E22.filletArc");var subQ6=sQuery(id+"F0.wireOp",EDGE,"E1.bottom");var subQ7=sQuery(id+"F0.wireOp",EDGE,"E1.right");var subQ8=sQuery(id+"F0.wireOp",EDGE,"E1.top");var subQ9=sQuery(id+"F0.wireOp",EDGE,"E1.left");var subQ10=sQuery(id+"F0.wireOp",EDGE,"E23.filletArc");var subQ11=sQuery(id+"F0.wireOp",EDGE,"E24.filletArc");Q0=makeQuery(id+"F2.boolean.opBoolean","SPLIT",FACE,{"disambiguationData":[TD([makeQuery(id+"F1.opExtrude","SWEPT_FACE",FACE,{"disambiguationData":[OSD([subQ6])]})])],"derivedFrom":makeQuery(id+"F1.opExtrude","CAP_FACE",FACE,{"disambiguationData":[OSD([subQ6,subQ8,subQ9,subQ7,subQ4,subQ3,subQ2,subQ1,subQ0,subQ5,subQ10,subQ11])],"isStart":true})});}
            var sketch = newSketch(context, id + "F16", { "sketchPlane" : qUnion([Q0])});
            skLineSegment(sketch, "E79", {"start": v(0, 90) * mm, "end": v(0, 120) * mm, "construction": true});
            skCircle(sketch, "E80", {"center": v(0, 120) * mm, "radius": 6 * mm});
            skLineSegment(sketch, "E81", {"start": v(-33, 90) * mm, "end": v(-15, 108) * mm});
            skLineSegment(sketch, "E82", {"start": v(-15, 108) * mm, "end": v(-15, 120) * mm});
            skLineSegment(sketch, "E83", {"start": v(33, 90) * mm, "end": v(15, 108) * mm});
            skLineSegment(sketch, "E84", {"start": v(15, 120) * mm, "end": v(15, 108) * mm});
            skArc(sketch, "E85", {"start": v(15, 120) * mm, "mid": v(0, 135) * mm, "end": v(-15, 120) * mm});
            skLineSegment(sketch, "E86", {"start": v(-80, 0) * mm, "end": v(80, 0) * mm, "construction": true});
            skLineSegment(sketch, "E87.MirrorCS", {"start": v(-33, -90) * mm, "end": v(-15, -108) * mm});
            skLineSegment(sketch, "E88.MirrorCS", {"start": v(-15, -108) * mm, "end": v(-15, -120) * mm});
            skArc(sketch, "E89.MirrorCS", {"start": v(15, -120) * mm, "mid": v(0, -135) * mm, "end": v(-15, -120) * mm});
            skLineSegment(sketch, "E90.MirrorCS", {"start": v(15, -120) * mm, "end": v(15, -108) * mm});
            skLineSegment(sketch, "E91.MirrorCS", {"start": v(33, -90) * mm, "end": v(15, -108) * mm});
            skLineSegment(sketch, "E92.MirrorCS", {"start": v(0, -90) * mm, "end": v(0, -120) * mm, "construction": true});
            skCircle(sketch, "E93.MirrorC", {"center": v(0, -120) * mm, "radius": 6 * mm});
            skSolve(sketch);
        }
        {
            var Q0;
            {var subQ1=sQuery(id+"F16.wireOp",EDGE,"E81");Q0=makeQuery(id+"F16.imprint","IMPRINT",FACE,{"disambiguationData":[TD([[makeQuery(id+"F16.imprint","IMPRINT",EDGE,{"derivedFrom":subQ1}),-1.0]])]});}
            var Q1;
            Q1=makeQuery(id+"F16.imprint","IMPRINT",FACE,{"disambiguationData":[TD([[makeQuery(id+"F16.imprint","IMPRINT",EDGE,{"derivedFrom":makeQuery(id+"F1.opExtrude","CAP_EDGE",EDGE,{"disambiguationData":[OSD([sQuery(id+"F0.wireOp",EDGE,"E1.left")])],"isStart":true})}),-1.0]])]});
            var Q2;
            {var subQ0=sQuery(id+"F16.wireOp",EDGE,"E87.MirrorCS");Q2=makeQuery(id+"F16.imprint","IMPRINT",FACE,{"disambiguationData":[TD([[makeQuery(id+"F16.imprint","IMPRINT",EDGE,{"derivedFrom":subQ0}),1.0]])]});}
            var Q3;
            Q3=makeQuery(id+"F2.opExtrude","CAP_FACE",FACE,{"disambiguationData":[OSD([sQuery(id+"F0.wireOp",EDGE,"E12"),sQuery(id+"F0.wireOp",EDGE,"E13"),sQuery(id+"F0.wireOp",EDGE,"E14"),sQuery(id+"F0.wireOp",EDGE,"E15"),sQuery(id+"F0.wireOp",EDGE,"E17.filletArc"),sQuery(id+"F0.wireOp",EDGE,"E18.filletArc"),sQuery(id+"F0.wireOp",EDGE,"E19.filletArc"),sQuery(id+"F0.wireOp",EDGE,"E20.filletArc"),sQuery(id+"F0.wireOp",EDGE,"E25.0"),sQuery(id+"F0.wireOp",EDGE,"E25.1"),sQuery(id+"F0.wireOp",EDGE,"E25.2"),sQuery(id+"F0.wireOp",EDGE,"E25.3"),sQuery(id+"F0.wireOp",EDGE,"E25.4"),sQuery(id+"F0.wireOp",EDGE,"E25.5"),sQuery(id+"F0.wireOp",EDGE,"E25.6"),sQuery(id+"F0.wireOp",EDGE,"E25.7")])],"isStart":false});
            extrude(context, id + "F17", {"entities" : qUnion([Q0, Q1, Q2]), "endBound" : BoundingType.UP_TO_SURFACE, "endBoundEntityFace" : qUnion([Q3]), "depth" : 25 * mm});
        }
    });
